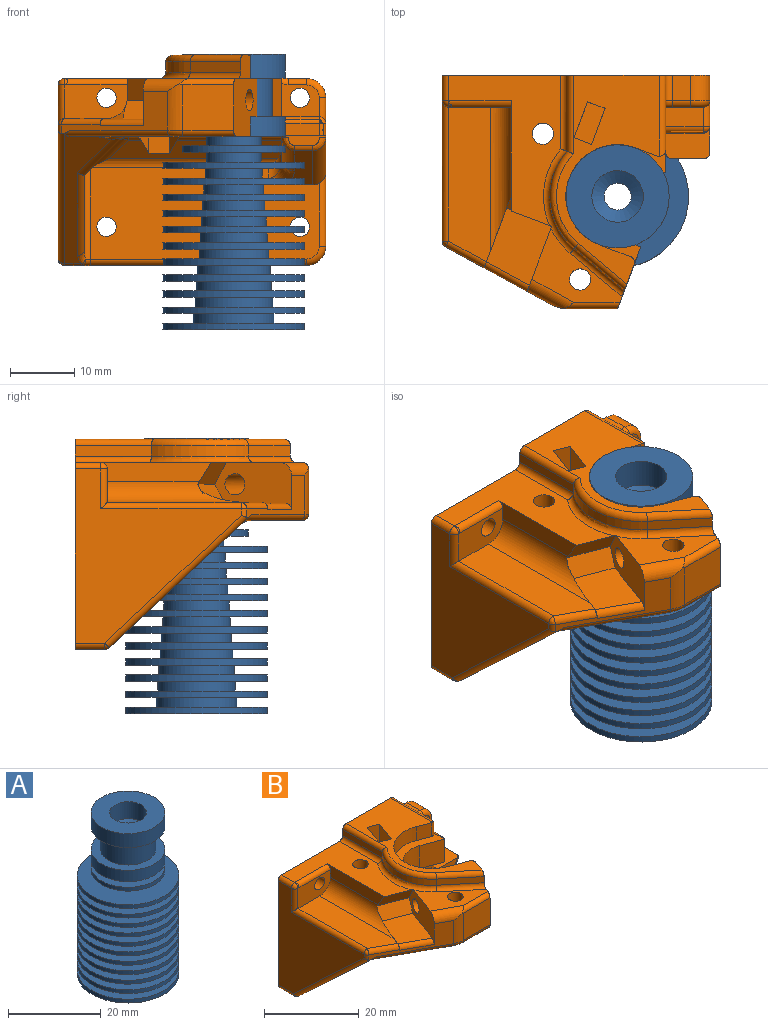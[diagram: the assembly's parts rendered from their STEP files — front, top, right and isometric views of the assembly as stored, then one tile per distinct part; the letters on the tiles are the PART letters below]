
ASSEMBLY  parts=2 mates=1
PART A: 62 faces, bbox 22x22x42.7 mm
  f0: cylinder r=3mm len=6mm, axis (0,0,-1), area 95mm2, adj f59,f60
  f1: cylinder r=2.1mm len=21.42mm, axis (0,0,1), area 282.6mm2, adj f57,f59
  f2: plane 22x22mm, normal (0,0,1), area 272.6mm2, adj f3,f56
  f3: cylinder r=5.85mm len=11.7mm, axis (0,0,1), area 55.1mm2, adj f2,f4
  f4: plane 22x22mm, normal (0,0,-1), area 272.6mm2, adj f3,f5
  f5: cylinder r=11mm len=22mm, axis (0,0,1), area 69.1mm2, adj f4,f6
  f6: plane 22x22mm, normal (0,0,1), area 279.8mm2, adj f5,f7
  f7: cylinder r=5.65mm len=11.3mm, axis (0,0,1), area 53.2mm2, adj f6,f8
  f8: plane 22x22mm, normal (0,0,-1), area 279.8mm2, adj f7,f9
  f9: cylinder r=11mm len=22mm, axis (0,0,1), area 69.1mm2, adj f8,f10
  f10: plane 22x22mm, normal (0,0,1), area 286.8mm2, adj f9,f11
  f11: cylinder r=5.45mm len=10.9mm, axis (0,0,1), area 51.4mm2, adj f10,f12
  f12: plane 22x22mm, normal (0,0,-1), area 286.8mm2, adj f11,f13
  f13: cylinder r=11mm len=22mm, axis (0,0,1), area 69.1mm2, adj f12,f14
  f14: plane 22x22mm, normal (0,0,1), area 293.5mm2, adj f13,f15
  f15: cylinder r=5.25mm len=10.5mm, axis (0,0,1), area 49.5mm2, adj f14,f16
  f16: plane 22x22mm, normal (0,0,-1), area 293.5mm2, adj f15,f17
  f17: cylinder r=11mm len=22mm, axis (0,0,1), area 69.1mm2, adj f16,f18
  f18: plane 22x22mm, normal (0,0,1), area 300mm2, adj f17,f19
  f19: cylinder r=5.05mm len=10.1mm, axis (0,0,1), area 47.6mm2, adj f18,f20
  f20: plane 22x22mm, normal (0,0,-1), area 300mm2, adj f19,f21
  f21: cylinder r=11mm len=22mm, axis (0,0,1), area 69.1mm2, adj f20,f22
  f22: plane 22x22mm, normal (0,0,1), area 306.2mm2, adj f21,f23
  f23: cylinder r=4.85mm len=9.7mm, axis (0,0,1), area 45.7mm2, adj f22,f24
  f24: plane 22x22mm, normal (0,0,-1), area 306.2mm2, adj f23,f25
  f25: cylinder r=11mm len=22mm, axis (0,0,1), area 69.1mm2, adj f24,f26
  f26: plane 22x22mm, normal (0,0,1), area 312.2mm2, adj f25,f27
  f27: cylinder r=4.65mm len=9.3mm, axis (0,0,1), area 43.8mm2, adj f26,f28
  f28: plane 22x22mm, normal (0,0,-1), area 312.2mm2, adj f27,f29
  f29: cylinder r=11mm len=22mm, axis (0,0,1), area 69.1mm2, adj f28,f30
  f30: plane 22x22mm, normal (0,0,1), area 317.9mm2, adj f29,f31
  f31: cylinder r=4.45mm len=8.9mm, axis (0,0,1), area 41.9mm2, adj f30,f32
  f32: plane 22x22mm, normal (0,0,-1), area 317.9mm2, adj f31,f33
  f33: cylinder r=11mm len=22mm, axis (0,0,1), area 69.1mm2, adj f32,f34
  f34: plane 22x22mm, normal (0,0,1), area 323.4mm2, adj f33,f35
  f35: cylinder r=4.25mm len=8.5mm, axis (0,0,1), area 40.1mm2, adj f34,f36
  f36: plane 16x16mm, normal (0,0,-1), area 144.3mm2, adj f35,f37
  f37: cylinder r=8mm len=16mm, axis (0,0,1), area 50.3mm2, adj f36,f38
  f38: plane 16x16mm, normal (0,0,1), area 144.3mm2, adj f37,f39
  f39: cylinder r=4.25mm len=8.5mm, axis (0,0,1), area 40.1mm2, adj f38,f40
  f40: plane 16x16mm, normal (0,0,-1), area 144.3mm2, adj f39,f41
  f41: cylinder r=8mm len=16mm, axis (0,0,1), area 150.8mm2, adj f40,f42
  f42: plane 16x16mm, normal (0,0,1), area 88mm2, adj f41,f43
  f43: cylinder r=6mm len=12mm, axis (0,0,1), area 226.2mm2, adj f42,f44
  f44: plane 16x16mm, normal (0,0,-1), area 88mm2, adj f43,f45
  f45: cylinder r=8mm len=16mm, axis (0,0,1), area 186mm2, adj f44,f46
  f46: plane 16x16mm, normal (0,0,1), area 150.8mm2, adj f45,f58
  f47: plane 22x22mm, normal (0,0,-1), area 349.9mm2, adj f48,f61
  f48: cylinder r=11mm len=22mm, axis (0,0,1), area 69.1mm2, adj f47,f49
  f49: plane 22x22mm, normal (0,0,1), area 257.4mm2, adj f48,f50
  f50: cylinder r=6.25mm len=12.5mm, axis (0,0,1), area 58.9mm2, adj f49,f51
  f51: plane 22x22mm, normal (0,0,-1), area 257.4mm2, adj f50,f52
  f52: cylinder r=11mm len=22mm, axis (0,0,1), area 69.1mm2, adj f51,f53
  f53: plane 22x22mm, normal (0,0,1), area 265.1mm2, adj f52,f54
  f54: cylinder r=6.05mm len=12.1mm, axis (0,0,1), area 57mm2, adj f53,f55
  f55: plane 22x22mm, normal (0,0,-1), area 265.1mm2, adj f54,f56
  f56: cylinder r=11mm len=22mm, axis (0,0,1), area 69.1mm2, adj f2,f55
  f57: cone r=0mm half-angle=59deg, axis (0,0,1), area 42.5mm2, adj f1,f58
  f58: cylinder r=4mm len=8mm, axis (0,0,1), area 113.1mm2, adj f46,f57
  f59: cone r=0mm half-angle=59deg, axis (0,0,-1), area 16.8mm2, adj f0,f1
  f60: cone r=0mm half-angle=59deg, axis (0,0,-1), area 2.2mm2, adj f0,f61
  f61: cylinder r=3.1mm len=10mm, axis (0,0,-1), area 194.8mm2, adj f47,f60
PART B: 144 faces, bbox 44.2x39.5x35.3 mm
  f0: plane 12.05x7.5mm, normal (-0.94,0.35,0), area 65.9mm2, adj f1,f136,f137,f138,f139,f140,f141,f142
  f1: cylinder r=1.65mm len=14.34mm, axis (0.94,-0.35,0), area 145.9mm2, adj f0,f2
  f2: plane 9.75x9.16mm, normal (0.94,-0.35,0), area 74mm2, adj f1,f3,f122,f123,f124,f125,f134,f135
  f3: cylinder r=1mm len=8.72mm, axis (1,0,0), area 12.3mm2, adj f2,f4,f135,f136,f137
  f4: cylinder r=5mm len=7.21mm, axis (0,0,-1), area 16.8mm2, adj f3,f5,f135,f137,f138
  f5: torus R=4mm, axis (0,0,1), area 3.6mm2, adj f4,f6,f125,f134
  f6: cylinder r=1mm len=16.39mm, axis (0.88,-0.48,0), area 28mm2, adj f5,f7,f125,f138
  f7: plane 22.71x21.32mm, normal (0,-0.68,-0.73), area 80.7mm2, adj f6,f8,f117,f118,f119,f120,f121,f125
  f8: bspline ~5.62x2.83mm, area 6.8mm2, adj f7,f9,f117,f125
  f9: cylinder r=2mm len=14.49mm, axis (0,-1,0), area 22.8mm2, adj f8,f10,f116,f125
  f10: plane 19.55x5.71mm, normal (0.71,0,-0.71), area 109mm2, adj f9,f11,f114,f115,f117,f118
  f11: cylinder r=2mm len=6.18mm, axis (-0.58,0.58,-0.58), area 14mm2, adj f10,f12,f112,f113,f114,f116
  f12: plane 35.91x14.6mm, normal (0,-1,0), area 468.4mm2, adj f11,f13,f104,f105,f106,f107,f108,f109
  f13: cylinder r=1.5mm len=4.97mm, axis (0,-1,0), area 46.9mm2, adj f12,f14
  f14: plane 41.5x32.61mm, normal (0,1,0), area 1226.5mm2, adj f13,f15,f51,f64,f66,f69,f70,f71
  f15: cylinder r=1.5mm len=4.97mm, axis (0,-1,0), area 46.9mm2, adj f14,f16
  f16: plane 5.83x5.23mm, normal (0,-1,0), area 21.1mm2, adj f15,f17,f18,f48,f49,f50,f74
  f17: torus R=2mm, axis (0,-1,0), area 6.5mm2, adj f16,f18,f50,f71
  f18: cylinder r=1mm len=3.96mm, axis (0,0,-1), area 5.4mm2, adj f16,f17,f19,f70
  f19: cylinder r=1mm len=4mm, axis (0,-1,0), area 5.5mm2, adj f18,f20,f48,f70
  f20: sphere r=1mm, area 0.6mm2, adj f19,f21,f47
  f21: cylinder r=1mm len=5.83mm, axis (-1,0,0), area 9.2mm2, adj f20,f22,f23,f48,f74
  f22: sphere r=1mm, area 0.2mm2, adj f21,f47
  f23: plane 5.83x1.95mm, normal (0,-1,0), area 11.4mm2, adj f21,f24,f47,f74
  f24: plane 6.83x5mm, normal (0,0,1), area 27.1mm2, adj f23,f25,f30,f45,f46,f47,f70,f74
  f25: cylinder r=1mm len=1mm, axis (0,0,1), area 0.4mm2, adj f24,f26,f30,f46
  f26: bspline ~2.04x2mm, area 3.1mm2, adj f25,f27,f29,f46
  f27: cylinder r=1mm len=2.83mm, axis (-1,0,0), area 2.7mm2, adj f26,f28,f46,f107
  f28: bspline ~2.04x2mm, area 3.1mm2, adj f27,f45,f46,f108
  f29: cylinder r=2mm len=6.15mm, axis (0,-0.82,0.57), area 18.1mm2, adj f26,f30,f106,f107
  f30: plane 5x3.76mm, normal (-1,0,0), area 7.6mm2, adj f24,f25,f29,f31,f41,f105,f113,f125
  f31: cylinder r=2mm len=16.25mm, axis (-1,0,0), area 25.2mm2, adj f30,f32,f40,f113,f125
  f32: plane 4.65x2.78mm, normal (-0.87,-0.5,0), area 10.4mm2, adj f31,f33,f38,f40,f113
  f33: plane 4.62x3.18mm, normal (0,-1,0), area 14.7mm2, adj f32,f34,f38,f113
  f34: plane 4.65x2.78mm, normal (0.87,-0.5,0), area 10.4mm2, adj f33,f35,f36,f38,f113
  f35: cylinder r=2mm len=2.07mm, axis (-1,0,0), area 2.9mm2, adj f34,f36,f113,f116,f125
  f36: plane 2.76x2.13mm, normal (0.87,0.5,0), area 6.4mm2, adj f34,f35,f37,f38,f125
  f37: plane 3.18x2mm, normal (0,1,0), area 6.4mm2, adj f36,f38,f40,f125
  f38: plane 6.35x5.5mm, normal (0,0,-1), area 17.6mm2, adj f32,f33,f34,f36,f37,f39,f40
  f39: cylinder r=1.65mm len=7mm, axis (0,0,1), area 72.6mm2, adj f38,f101
  f40: plane 2.76x2.13mm, normal (-0.87,0.5,0), area 6.4mm2, adj f31,f32,f37,f38,f125
  f41: cylinder r=1mm len=3.08mm, axis (0,0,-1), area 5.9mm2, adj f30,f42,f74,f123,f125
  f42: plane 3.28x3.08mm, normal (-0.35,-0.94,0), area 10.8mm2, adj f41,f43,f123,f125
  f43: cylinder r=8.05mm len=15.59mm, axis (0,0,1), area 77.9mm2, adj f42,f44,f123,f125
  f44: plane 4.8x3.08mm, normal (0.35,0.94,0), area 15.8mm2, adj f43,f123,f124,f125
  f45: cylinder r=1mm len=1mm, axis (0,0,1), area 0.4mm2, adj f24,f28,f46,f70
  f46: plane 4.83x1.48mm, normal (0,-1,0), area 6.6mm2, adj f24,f25,f26,f27,f28,f45
  f47: cylinder r=1mm len=1.95mm, axis (0,0,-1), area 3.1mm2, adj f20,f22,f23,f24,f70
  f48: plane 5.83x3mm, normal (0,0,1), area 17.5mm2, adj f16,f19,f21,f74
  f49: torus R=2mm, axis (0,-1,0), area 2.1mm2, adj f16,f50,f73,f74
  f50: cylinder r=1mm len=2.83mm, axis (1,0,0), area 4.4mm2, adj f16,f17,f49,f72
  f51: cylinder r=1.5mm len=4.97mm, axis (0,-1,0), area 46.9mm2, adj f14,f52
  f52: plane 9.7x5.2mm, normal (0,-1,0), area 41.2mm2, adj f51,f53,f54,f60,f61,f63
  f53: plane 17.11x3mm, normal (-1,0,0), area 45.8mm2, adj f52,f54,f63,f101,f142
  f54: cylinder r=3.2mm len=22.24mm, axis (0,-1,0), area 84.9mm2, adj f52,f53,f55,f60,f141,f142
  f55: plane 10.45x3.97mm, normal (0.94,-0.35,0), area 4.8mm2, adj f54,f56,f60,f138,f139,f140,f141
  f56: cylinder r=1mm len=6.45mm, axis (-0.88,0.48,0), area 10.6mm2, adj f55,f57,f60,f138
  f57: sphere r=1mm, area 0.8mm2, adj f56,f58,f59
  f58: cylinder r=1mm len=1.36mm, axis (0,0,-1), area 1.3mm2, adj f57,f103,f121,f138
  f59: cylinder r=1mm len=21.77mm, axis (0,1,0), area 33.4mm2, adj f57,f60,f61,f103
  f60: plane 23.97x6.5mm, normal (0,0,1), area 145.9mm2, adj f52,f54,f55,f56,f59
  f61: cylinder r=1mm len=6.2mm, axis (0,0,1), area 9mm2, adj f52,f59,f62,f103
  f62: sphere r=1mm, area 2.1mm2, adj f61,f63,f102
  f63: cylinder r=1mm len=9.7mm, axis (1,0,0), area 15.2mm2, adj f52,f53,f62,f101
  f64: cylinder r=1mm len=4.58mm, axis (0,1,0), area 7.2mm2, adj f14,f65,f66,f103
  f65: sphere r=1mm, area 0.8mm2, adj f64,f120,f121
  f66: plane 37.5x4.58mm, normal (0,0,-1), area 150.8mm2, adj f14,f64,f67,f69,f111,f120
  f67: torus R=2mm, axis (0,0,1), area 1.7mm2, adj f66,f68,f111,f114
  f68: sphere r=1mm, area 0.2mm2, adj f67,f119,f120
  f69: cylinder r=3mm len=3.97mm, axis (0,1,0), area 18.7mm2, adj f14,f66,f70,f110
  f70: plane 23.01x11.97mm, normal (1,0,0), area 123.7mm2, adj f14,f18,f19,f24,f45,f47,f69,f71
  f71: cylinder r=3mm len=3.97mm, axis (0,1,0), area 18.7mm2, adj f14,f17,f70,f72
  f72: plane 3.97x2.83mm, normal (0,0,1), area 11.2mm2, adj f14,f50,f71,f73
  f73: cylinder r=1mm len=3.97mm, axis (0,1,0), area 6.2mm2, adj f14,f49,f72,f74
  f74: plane 17.63x14mm, normal (1,0,0), area 84.9mm2, adj f14,f16,f21,f23,f24,f41,f48,f49
  f75: cylinder r=1.65mm len=12.22mm, axis (0.94,-0.35,0), area 122.5mm2, adj f74,f76
  f76: plane 10.62x5.59mm, normal (-0.94,0.35,0), area 54.9mm2, adj f75,f77,f81,f82,f97
  f77: plane 10.62x2.71mm, normal (0.35,0.94,0), area 30.8mm2, adj f76,f78,f81,f97
  f78: plane 10.62x5.59mm, normal (0.94,-0.35,0), area 54.9mm2, adj f77,f79,f81,f82,f97
  f79: cylinder r=1.65mm len=8.32mm, axis (0.94,-0.35,0), area 79.3mm2, adj f78,f80
  f80: plane 3.3x3.09mm, normal (0.94,-0.35,0), area 8.6mm2, adj f79
  f81: plane 6.61x4.82mm, normal (0,0,1), area 17.3mm2, adj f76,f77,f78,f82
  f82: plane 10.62x2.71mm, normal (-0.35,-0.94,0), area 30.8mm2, adj f76,f78,f81,f97
  f83: plane 5.92x5.33mm, normal (-0.35,-0.94,0), area 33.7mm2, adj f74,f84,f123,f136
  f84: cylinder r=6.05mm len=11.71mm, axis (0,0,1), area 112.5mm2, adj f83,f122,f123,f136
  f85: cylinder r=1mm len=3.6mm, axis (0,0,-1), area 6.4mm2, adj f74,f86,f96,f97,f136
  f86: plane 3.6x3.28mm, normal (-0.35,-0.94,0), area 12.6mm2, adj f85,f87,f97,f136
  f87: cylinder r=8.05mm len=15.59mm, axis (0,0,-1), area 91mm2, adj f86,f88,f97,f136
  f88: plane 4.8x3.6mm, normal (0.35,0.94,0), area 18.5mm2, adj f87,f89,f97,f136
  f89: cylinder r=1mm len=3.6mm, axis (0,0,-1), area 5.7mm2, adj f88,f90,f97,f136
  f90: plane 5.08x3.75mm, normal (0.94,-0.35,0), area 15.2mm2, adj f89,f91,f92,f95,f97,f136
  f91: cylinder r=1mm len=8.71mm, axis (-0.77,0.64,0), area 16.2mm2, adj f90,f92,f136,f143
  f92: plane 7.8x6.51mm, normal (-0.64,-0.77,0), area 16.3mm2, adj f90,f91,f93,f95
  f93: cylinder r=10.5mm len=15.06mm, axis (0,0,-1), area 27mm2, adj f92,f94,f99,f143
  f94: torus R=9.5mm, axis (0,0,1), area 25.9mm2, adj f93,f95,f97,f98
  f95: cylinder r=1mm len=8.44mm, axis (-0.77,0.64,0), area 15.7mm2, adj f90,f92,f94,f97
  f96: cylinder r=1mm len=12.57mm, axis (0,-1,0), area 19mm2, adj f14,f74,f85,f97
  f97: plane 32.38x15.96mm, normal (0,0,1), area 181.3mm2, adj f14,f76,f77,f78,f82,f85,f86,f87
  f98: cylinder r=1mm len=12.2mm, axis (0,1,0), area 18.9mm2, adj f14,f94,f97,f99
  f99: plane 11.8x1.6mm, normal (-1,0,0), area 18.9mm2, adj f14,f93,f98,f100
  f100: cylinder r=1mm len=11.8mm, axis (0,-1,0), area 18.2mm2, adj f14,f99,f101,f143
  f101: plane 23.31x17.38mm, normal (0,0,1), area 178.3mm2, adj f14,f39,f53,f63,f100,f102,f142,f143
  f102: cylinder r=1mm len=3.97mm, axis (0,1,0), area 6.2mm2, adj f14,f62,f101,f103
  f103: plane 27.01x25.74mm, normal (-1,0,0), area 350.5mm2, adj f14,f58,f59,f61,f64,f102,f121
  f104: cylinder r=1.5mm len=4.97mm, axis (0,-1,0), area 46.9mm2, adj f12,f14
  f105: cylinder r=2mm len=4.48mm, axis (0,0,-1), area 5.2mm2, adj f12,f30,f106,f112,f113
  f106: bspline ~4.44x4.04mm, area 10.8mm2, adj f12,f29,f105,f107
  f107: plane 7.57x5.3mm, normal (0,-0.57,-0.82), area 28mm2, adj f12,f27,f29,f106,f108
  f108: cylinder r=2mm len=9.29mm, axis (0,0.82,-0.57), area 29.7mm2, adj f12,f28,f70,f107,f109
  f109: cylinder r=1mm len=11.24mm, axis (0,0,-1), area 16.5mm2, adj f12,f70,f108,f110
  f110: torus R=2mm, axis (0,-1,0), area 6.5mm2, adj f12,f69,f109,f111
  f111: cylinder r=1mm len=33.5mm, axis (-1,0,0), area 52.6mm2, adj f12,f66,f67,f110
  f112: cylinder r=2mm len=28.81mm, axis (-1,0,0), area 42mm2, adj f11,f12,f105,f113
  f113: plane 26.79x2.95mm, normal (0,-0.71,-0.71), area 88.1mm2, adj f11,f30,f31,f32,f33,f34,f35,f105
  f114: cylinder r=1mm len=13.98mm, axis (0,0,1), area 20.6mm2, adj f10,f11,f12,f67,f115,f119
  f115: plane 12.49x11.71mm, normal (1,0,0), area 73.1mm2, adj f10,f114,f118
  f116: sphere r=2mm, area 1.2mm2, adj f9,f11,f35
  f117: cylinder r=2mm len=7.24mm, axis (0.56,-0.6,0.56), area 19.1mm2, adj f7,f8,f10,f118
  f118: cylinder r=1mm len=14.35mm, axis (0,0.73,-0.68), area 28.1mm2, adj f7,f10,f115,f117,f119
  f119: bspline ~2.04x1.4mm, area 2.2mm2, adj f7,f68,f114,f118
  f120: cylinder r=1mm len=2.57mm, axis (1,0,0), area 1.9mm2, adj f7,f65,f66,f68
  f121: cylinder r=1mm len=22.3mm, axis (0,-0.73,0.68), area 46mm2, adj f7,f58,f65,f103,f138
  f122: plane 5.92x5.74mm, normal (0.35,0.94,0), area 36.3mm2, adj f2,f84,f123,f136
  f123: plane 18.68x15.51mm, normal (0,0,-1), area 67.9mm2, adj f2,f41,f42,f43,f44,f74,f83,f84
  f124: cylinder r=1mm len=3.08mm, axis (0,0,1), area 4.8mm2, adj f2,f44,f123,f125
  f125: plane 32.59x25.42mm, normal (0,0,-1), area 308.1mm2, adj f2,f5,f6,f7,f8,f9,f30,f31
  f126: plane 2.75x2mm, normal (0.87,0.5,0), area 6.4mm2, adj f125,f127,f129,f133
  f127: plane 6.35x5.5mm, normal (0,0,-1), area 17.6mm2, adj f126,f128,f129,f130,f131,f132,f133
  f128: cylinder r=1.65mm len=7mm, axis (0,0,1), area 72.6mm2, adj f127,f136
  f129: plane 2.75x2mm, normal (0.87,-0.5,0), area 6.4mm2, adj f125,f126,f127,f130
  f130: plane 3.18x2mm, normal (0,-1,0), area 6.4mm2, adj f125,f127,f129,f131
  f131: plane 2.75x2mm, normal (-0.87,-0.5,0), area 6.4mm2, adj f125,f127,f130,f132
  f132: plane 2.75x2mm, normal (-0.87,0.5,0), area 6.4mm2, adj f125,f127,f131,f133
  f133: plane 3.18x2mm, normal (0,1,0), area 6.4mm2, adj f125,f126,f127,f132
  f134: cylinder r=1mm len=8.25mm, axis (1,0,0), area 12.7mm2, adj f2,f5,f125,f135
  f135: plane 7.87x7mm, normal (0,-1,0), area 55.1mm2, adj f2,f3,f4,f134
  f136: plane 24.46x20.78mm, normal (0,0,1), area 131.4mm2, adj f0,f2,f3,f74,f83,f84,f85,f86
  f137: cylinder r=2mm len=7.47mm, axis (0.88,-0.48,0), area 19.6mm2, adj f0,f3,f4,f136,f138
  f138: plane 16.48x9.06mm, normal (-0.48,-0.88,0), area 36.7mm2, adj f0,f4,f6,f7,f55,f56,f58,f121
  f139: cylinder r=1mm len=7.29mm, axis (-0.88,0.48,0), area 12mm2, adj f0,f55,f138,f140
  f140: plane 12.03x10.21mm, normal (0,0,1), area 71.5mm2, adj f0,f55,f139,f141
  f141: plane 7.71x4.27mm, normal (-0.3,-0.81,0.5), area 25.8mm2, adj f0,f54,f55,f140,f142
  f142: plane 7x4.48mm, normal (-0.3,-0.81,-0.5), area 27.6mm2, adj f0,f53,f54,f101,f141,f143
  f143: torus R=11.5mm, axis (0,0,-1), area 27mm2, adj f0,f91,f93,f100,f101,f136,f142
PLACE A t=(-65.7,-9.87,64.86)mm
PLACE B t=(32.79,-58.66,26.87)mm fixed
MATE fastened A.f0 <-> B.f43  axis (0,0,1) through (-65.7,-9.87,58.16)mm
